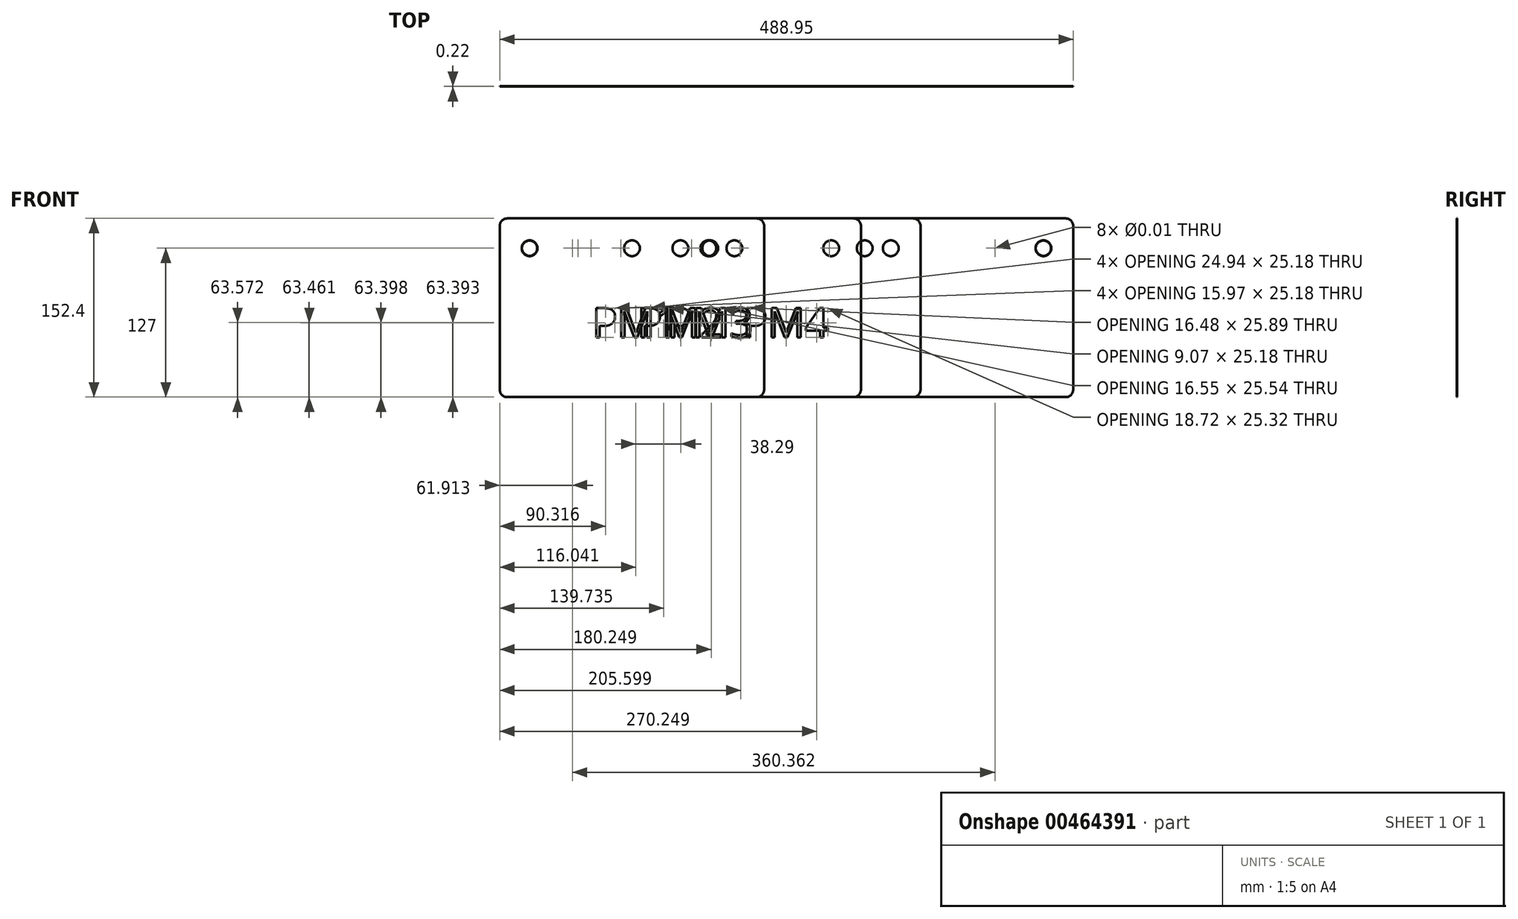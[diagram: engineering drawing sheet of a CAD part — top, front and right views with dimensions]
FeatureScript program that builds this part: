
annotation { "Feature Type Name" : "Feature", "Feature Type Description" : "" }
export const myFeature = defineFeature(function(context is Context, id is Id, definition is map)
    precondition{}
    {
        {
            assignVariable(context, id + "F0", {"name" : "Thickness", "anyValue" : .22});
        }
        {
            var Q0;
            Q0=qCreatedBy(makeId("Front.planeOp"),FACE);
            var sketch = newSketch(context, id + "F1", { "sketchPlane" : qUnion([Q0])});
            skLineSegment(sketch, "E0.bottom", {"start": v(0, -152.4) * mm, "end": v(488.95, -152.4) * mm});
            skLineSegment(sketch, "E0.top", {"start": v(0, 0) * mm, "end": v(488.95, 0) * mm});
            skLineSegment(sketch, "E0.left", {"start": v(0, -152.4) * mm, "end": v(0, 0) * mm});
            skLineSegment(sketch, "E0.right", {"start": v(488.95, -152.4) * mm, "end": v(488.95, 0) * mm});
            skPoint(sketch, "E1", {"position": v(25.4, -25.4) * mm});
            skPoint(sketch, "E2", {"position": v(66.68, -25.4) * mm});
            skPoint(sketch, "E3", {"position": v(244.48, -25.4) * mm});
            skPoint(sketch, "E4", {"position": v(422.28, -25.4) * mm});
            skPoint(sketch, "E5", {"position": v(463.55, -25.4) * mm});
            skLineSegment(sketch, "E6", {"start": v(244.48, 0) * mm, "end": v(244.48, -152.4) * mm, "construction": true});
            skText(sketch, "E7", { "text": "PM4", "fontName": "OpenSans-Regular.ttf"});
            skPoint(sketch, "E8", {"position": v(177.8, -25.4) * mm});
            skPoint(sketch, "E9", {"position": v(311.15, -25.4) * mm});
            const initialGuessF1  = {"E7": [0.20706, -0.1016, 1, 0, 0.0254]};
            skSetInitialGuess(sketch, initialGuessF1);
            skSolve(sketch);
        }
        {
            var Q0;
            Q0=makeQuery(id+"F1.imprint","IMPRINT",FACE,{"disambiguationData":[TD([[makeQuery(id+"F1.imprint","IMPRINT",EDGE,{"derivedFrom":sQuery(id+"F1.wireOp",EDGE,"E0.bottom")}),1.0]])]});
            extrude(context, id + "F2", {"entities" : qUnion([Q0]), "oppositeDirection" : true, "depth" : (getVariable(context, 'Thickness')) * mm});
        }
        {
            var Q0;
            Q0=sQuery(id+"F1.wireOp",VERTEX,"E2");
            var Q1;
            Q1=sQuery(id+"F1.wireOp",VERTEX,"E4");
            var Q2;
            Q2=makeQuery(id+"F2.opExtrude","SWEPT_BODY",BODY,{"disambiguationData":[OSD([sQuery(id+"F1.wireOp",EDGE,"E0.bottom"),sQuery(id+"F1.wireOp",EDGE,"E0.top"),sQuery(id+"F1.wireOp",EDGE,"E0.left"),sQuery(id+"F1.wireOp",EDGE,"E0.right")])]});
            hole(context, id + "F3", {"style" : HoleStyle.SIMPLE, "endStyle" : HoleEndStyle.THROUGH, "standardTappedOrClearance" : lookupTablePath({ "standard" : "ANSI", "size" : "3/8 (0.38)", "type" : "Drilled" }), "standardBlindInLast" : lookupTablePath({ "standard" : "ANSI", "size" : "3/8", "type" : "Drilled" }), "holeDiameter" : 3 / 203.2 * mm, "isTappedThrough" : true, "tappedDepth" : 12.7 * mm, "tapClearance" : 3, "locations" : qUnion([Q0, Q1]), "scope" : qUnion([Q2])});
        }
        {
            var Q0;
            Q0=sQuery(id+"F1.wireOp",VERTEX,"E1");
            var Q1;
            Q1=sQuery(id+"F1.wireOp",VERTEX,"E5");
            var Q2;
            Q2=sQuery(id+"F1.wireOp",VERTEX,"E9");
            var Q3;
            Q3=sQuery(id+"F1.wireOp",VERTEX,"E8");
            var Q4;
            Q4=makeQuery(id+"F2.opExtrude","SWEPT_BODY",BODY,{"disambiguationData":[OSD([sQuery(id+"F1.wireOp",EDGE,"E0.bottom"),sQuery(id+"F1.wireOp",EDGE,"E0.top"),sQuery(id+"F1.wireOp",EDGE,"E0.left"),sQuery(id+"F1.wireOp",EDGE,"E0.right")])]});
            hole(context, id + "F4", {"style" : HoleStyle.C_SINK, "endStyle" : HoleEndStyle.THROUGH, "standardTappedOrClearance" : lookupTablePath({ "standard" : "ISO", "fit" : "Normal", "size" : "M6", "type" : "Clearance" }), "standardBlindInLast" : lookupTablePath({ "fit" : "Standard", "standard" : "ISO", "size" : "M6", "type" : "Clearance" }), "holeDiameter" : 6.6 * mm, "cSinkDiameter" : 13.44 * mm, "cSinkAngle" : 90 * degree, "isTappedThrough" : true, "tappedDepth" : 12.7 * mm, "tapClearance" : 3, "locations" : qUnion([Q0, Q1, Q2, Q3]), "scope" : qUnion([Q4])});
        }
        {
            var Q0;
            Q0=makeQuery(id+"F2.opExtrude","SWEPT_EDGE",EDGE,{"disambiguationData":[OSD([sQuery(id+"F1.wireOp",EDGE,"E0.top"),sQuery(id+"F1.wireOp",EDGE,"E0.left")])]});
            var Q1;
            Q1=makeQuery(id+"F2.opExtrude","SWEPT_EDGE",EDGE,{"disambiguationData":[OSD([sQuery(id+"F1.wireOp",EDGE,"E0.top"),sQuery(id+"F1.wireOp",EDGE,"E0.right")])]});
            var Q2;
            Q2=makeQuery(id+"F2.opExtrude","SWEPT_EDGE",EDGE,{"disambiguationData":[OSD([sQuery(id+"F1.wireOp",EDGE,"E0.bottom"),sQuery(id+"F1.wireOp",EDGE,"E0.right")])]});
            var Q3;
            Q3=makeQuery(id+"F2.opExtrude","SWEPT_EDGE",EDGE,{"disambiguationData":[OSD([sQuery(id+"F1.wireOp",EDGE,"E0.bottom"),sQuery(id+"F1.wireOp",EDGE,"E0.left")])]});
            fillet(context, id + "F5", {"entities" : qUnion([Q0, Q1, Q2, Q3]), "radius" : 6.35 * mm, "tangentPropagation" : true, "allowEdgeOverflow" : false});
        }
        {
            var Q0;
            Q0=qCreatedBy(makeId("Front.planeOp"),FACE);
            var sketch = newSketch(context, id + "F6", { "sketchPlane" : qUnion([Q0])});
            skLineSegment(sketch, "E10.bottom", {"start": v(0, -152.4) * mm, "end": v(358.77, -152.4) * mm});
            skLineSegment(sketch, "E10.top", {"start": v(0, 0) * mm, "end": v(358.78, 0) * mm});
            skLineSegment(sketch, "E10.left", {"start": v(0, -152.4) * mm, "end": v(0, 0) * mm});
            skLineSegment(sketch, "E10.right", {"start": v(358.78, -152.4) * mm, "end": v(358.78, 0) * mm});
            skLineSegment(sketch, "E11", {"start": v(179.39, 0) * mm, "end": v(179.39, -152.4) * mm, "construction": true});
            skPoint(sketch, "E12", {"position": v(25.4, -25.4) * mm});
            skPoint(sketch, "E13", {"position": v(77.79, -25.4) * mm});
            skPoint(sketch, "E14", {"position": v(179.39, -25.4) * mm});
            skPoint(sketch, "E15", {"position": v(280.99, -25.4) * mm});
            skPoint(sketch, "E16", {"position": v(333.38, -25.4) * mm});
            skText(sketch, "E17", { "text": "PM3", "fontName": "OpenSans-Regular.ttf"});
            const initialGuessF6  = {"E17": [0.14265, -0.1016, 1, 0, 0.0254]};
            skSetInitialGuess(sketch, initialGuessF6);
            skSolve(sketch);
        }
        {
            var Q0;
            Q0 = qSketchRegion(id + "F6", true);
            extrude(context, id + "F7", {"entities" : qUnion([Q0]), "oppositeDirection" : true, "depth" : (getVariable(context, 'Thickness')) * mm});
        }
        {
            var Q0;
            Q0=makeQuery(id+"F7.opExtrude","SWEPT_EDGE",EDGE,{"disambiguationData":[OSD([sQuery(id+"F6.wireOp",EDGE,"E10.top"),sQuery(id+"F6.wireOp",EDGE,"E10.left")])]});
            var Q1;
            Q1=makeQuery(id+"F7.opExtrude","SWEPT_EDGE",EDGE,{"disambiguationData":[OSD([sQuery(id+"F6.wireOp",EDGE,"E10.top"),sQuery(id+"F6.wireOp",EDGE,"E10.right")])]});
            var Q2;
            Q2=makeQuery(id+"F7.opExtrude","SWEPT_EDGE",EDGE,{"disambiguationData":[OSD([sQuery(id+"F6.wireOp",EDGE,"E10.bottom"),sQuery(id+"F6.wireOp",EDGE,"E10.right")])]});
            var Q3;
            Q3=makeQuery(id+"F7.opExtrude","SWEPT_EDGE",EDGE,{"disambiguationData":[OSD([sQuery(id+"F6.wireOp",EDGE,"E10.bottom"),sQuery(id+"F6.wireOp",EDGE,"E10.left")])]});
            fillet(context, id + "F8", {"entities" : qUnion([Q0, Q1, Q2, Q3]), "radius" : 6.35 * mm, "tangentPropagation" : true, "allowEdgeOverflow" : false});
        }
        {
            var Q0;
            Q0=sQuery(id+"F6.wireOp",VERTEX,"E15");
            var Q1;
            Q1=sQuery(id+"F6.wireOp",VERTEX,"E13");
            var Q2;
            Q2=makeQuery(id+"F7.opExtrude","SWEPT_BODY",BODY,{"disambiguationData":[OSD([sQuery(id+"F6.wireOp",EDGE,"E10.bottom"),sQuery(id+"F6.wireOp",EDGE,"E10.top"),sQuery(id+"F6.wireOp",EDGE,"E10.left"),sQuery(id+"F6.wireOp",EDGE,"E10.right")])]});
            hole(context, id + "F9", {"style" : HoleStyle.SIMPLE, "endStyle" : HoleEndStyle.THROUGH, "standardTappedOrClearance" : lookupTablePath({ "standard" : "ANSI", "size" : "3/8 (0.38)", "type" : "Drilled" }), "standardBlindInLast" : lookupTablePath({ "standard" : "ANSI", "size" : "3/8", "type" : "Drilled" }), "holeDiameter" : 3 / 203.2 * mm, "isTappedThrough" : true, "tappedDepth" : 12.7 * mm, "tapClearance" : 3, "locations" : qUnion([Q0, Q1]), "scope" : qUnion([Q2])});
        }
        {
            var Q0;
            Q0=sQuery(id+"F6.wireOp",VERTEX,"E12");
            var Q1;
            Q1=sQuery(id+"F6.wireOp",VERTEX,"E14");
            var Q2;
            Q2=sQuery(id+"F6.wireOp",VERTEX,"E16");
            var Q3;
            Q3=makeQuery(id+"F7.opExtrude","SWEPT_BODY",BODY,{"disambiguationData":[OSD([sQuery(id+"F6.wireOp",EDGE,"E10.bottom"),sQuery(id+"F6.wireOp",EDGE,"E10.top"),sQuery(id+"F6.wireOp",EDGE,"E10.left"),sQuery(id+"F6.wireOp",EDGE,"E10.right")])]});
            hole(context, id + "F10", {"style" : HoleStyle.C_SINK, "endStyle" : HoleEndStyle.THROUGH, "standardTappedOrClearance" : lookupTablePath({ "standard" : "ISO", "fit" : "Normal", "size" : "M6", "type" : "Clearance" }), "standardBlindInLast" : lookupTablePath({ "fit" : "Standard", "standard" : "ISO", "size" : "M6", "type" : "Clearance" }), "holeDiameter" : 6.6 * mm, "cSinkDiameter" : 13.44 * mm, "cSinkAngle" : 90 * degree, "isTappedThrough" : true, "tappedDepth" : 12.7 * mm, "tapClearance" : 3, "locations" : qUnion([Q0, Q1, Q2]), "scope" : qUnion([Q3])});
        }
        {
            var Q0;
            Q0=qCreatedBy(makeId("Front.planeOp"),FACE);
            var sketch = newSketch(context, id + "F11", { "sketchPlane" : qUnion([Q0])});
            skLineSegment(sketch, "E18.bottom", {"start": v(0, -152.4) * mm, "end": v(307.97, -152.4) * mm});
            skLineSegment(sketch, "E18.top", {"start": v(0, 0) * mm, "end": v(307.97, 0) * mm});
            skLineSegment(sketch, "E18.left", {"start": v(0, -152.4) * mm, "end": v(0, 0) * mm});
            skLineSegment(sketch, "E18.right", {"start": v(307.98, -152.4) * mm, "end": v(307.98, 0) * mm});
            skLineSegment(sketch, "E19", {"start": v(153.99, 0) * mm, "end": v(153.99, -152.4) * mm, "construction": true});
            skPoint(sketch, "E20", {"position": v(103.19, -25.4) * mm});
            skPoint(sketch, "E21", {"position": v(204.79, -25.4) * mm});
            skPoint(sketch, "E22", {"position": v(25.4, -25.4) * mm});
            skPoint(sketch, "E23", {"position": v(153.99, -25.4) * mm});
            skPoint(sketch, "E24", {"position": v(282.57, -25.4) * mm});
            skText(sketch, "E25", { "text": "PM2", "fontName": "OpenSans-Regular.ttf"});
            const initialGuessF11  = {"E25": [0.11716, -0.1016, 1, 0, 0.0254]};
            skSetInitialGuess(sketch, initialGuessF11);
            skSolve(sketch);
        }
        {
            var Q0;
            Q0=makeQuery(id+"F11.imprint","IMPRINT",FACE,{"disambiguationData":[TD([[makeQuery(id+"F11.imprint","IMPRINT",EDGE,{"derivedFrom":sQuery(id+"F11.wireOp",EDGE,"E18.bottom")}),1.0]])]});
            extrude(context, id + "F12", {"entities" : qUnion([Q0]), "oppositeDirection" : true, "depth" : (getVariable(context, 'Thickness')) * mm});
        }
        {
            var Q0;
            Q0=makeQuery(id+"F12.opExtrude","SWEPT_EDGE",EDGE,{"disambiguationData":[OSD([sQuery(id+"F11.wireOp",EDGE,"E18.top"),sQuery(id+"F11.wireOp",EDGE,"E18.left")])]});
            var Q1;
            Q1=makeQuery(id+"F12.opExtrude","SWEPT_EDGE",EDGE,{"disambiguationData":[OSD([sQuery(id+"F11.wireOp",EDGE,"E18.top"),sQuery(id+"F11.wireOp",EDGE,"E18.right")])]});
            var Q2;
            Q2=makeQuery(id+"F12.opExtrude","SWEPT_EDGE",EDGE,{"disambiguationData":[OSD([sQuery(id+"F11.wireOp",EDGE,"E18.bottom"),sQuery(id+"F11.wireOp",EDGE,"E18.right")])]});
            var Q3;
            Q3=makeQuery(id+"F12.opExtrude","SWEPT_EDGE",EDGE,{"disambiguationData":[OSD([sQuery(id+"F11.wireOp",EDGE,"E18.bottom"),sQuery(id+"F11.wireOp",EDGE,"E18.left")])]});
            fillet(context, id + "F13", {"entities" : qUnion([Q0, Q1, Q2, Q3]), "radius" : 6.35 * mm, "tangentPropagation" : true, "allowEdgeOverflow" : false});
        }
        {
            var Q0;
            Q0=sQuery(id+"F11.wireOp",VERTEX,"E21");
            var Q1;
            Q1=sQuery(id+"F11.wireOp",VERTEX,"E20");
            var Q2;
            Q2=makeQuery(id+"F12.opExtrude","SWEPT_BODY",BODY,{"disambiguationData":[OSD([sQuery(id+"F11.wireOp",EDGE,"E18.bottom"),sQuery(id+"F11.wireOp",EDGE,"E18.top"),sQuery(id+"F11.wireOp",EDGE,"E18.left"),sQuery(id+"F11.wireOp",EDGE,"E18.right")])]});
            hole(context, id + "F14", {"style" : HoleStyle.SIMPLE, "endStyle" : HoleEndStyle.THROUGH, "standardTappedOrClearance" : lookupTablePath({ "standard" : "ANSI", "size" : "3/8 (0.38)", "type" : "Drilled" }), "standardBlindInLast" : lookupTablePath({ "standard" : "ANSI", "size" : "3/8", "type" : "Drilled" }), "holeDiameter" : 3 / 203.2 * mm, "isTappedThrough" : true, "tappedDepth" : 12.7 * mm, "tapClearance" : 3, "locations" : qUnion([Q0, Q1]), "scope" : qUnion([Q2])});
        }
        {
            var Q0;
            Q0=sQuery(id+"F11.wireOp",VERTEX,"E22");
            var Q1;
            Q1=sQuery(id+"F11.wireOp",VERTEX,"E23");
            var Q2;
            Q2=sQuery(id+"F11.wireOp",VERTEX,"E24");
            var Q3;
            Q3=makeQuery(id+"F12.opExtrude","SWEPT_BODY",BODY,{"disambiguationData":[OSD([sQuery(id+"F11.wireOp",EDGE,"E18.bottom"),sQuery(id+"F11.wireOp",EDGE,"E18.top"),sQuery(id+"F11.wireOp",EDGE,"E18.left"),sQuery(id+"F11.wireOp",EDGE,"E18.right"),sQuery(id+"F11.wireOp",EDGE,"E25.sketch_text.stroke-0"),sQuery(id+"F11.wireOp",EDGE,"E25.sketch_text.stroke-1"),sQuery(id+"F11.wireOp",EDGE,"E25.sketch_text.stroke-2"),sQuery(id+"F11.wireOp",EDGE,"E25.sketch_text.stroke-3"),sQuery(id+"F11.wireOp",EDGE,"E25.sketch_text.stroke-4"),sQuery(id+"F11.wireOp",EDGE,"E25.sketch_text.stroke-5"),sQuery(id+"F11.wireOp",EDGE,"E25.sketch_text.stroke-6"),sQuery(id+"F11.wireOp",EDGE,"E25.sketch_text.stroke-7"),sQuery(id+"F11.wireOp",EDGE,"E25.sketch_text.stroke-15"),sQuery(id+"F11.wireOp",EDGE,"E25.sketch_text.stroke-16"),sQuery(id+"F11.wireOp",EDGE,"E25.sketch_text.stroke-17"),sQuery(id+"F11.wireOp",EDGE,"E25.sketch_text.stroke-18"),sQuery(id+"F11.wireOp",EDGE,"E25.sketch_text.stroke-19"),sQuery(id+"F11.wireOp",EDGE,"E25.sketch_text.stroke-20"),sQuery(id+"F11.wireOp",EDGE,"E25.sketch_text.stroke-21"),sQuery(id+"F11.wireOp",EDGE,"E25.sketch_text.stroke-22"),sQuery(id+"F11.wireOp",EDGE,"E25.sketch_text.stroke-23"),sQuery(id+"F11.wireOp",EDGE,"E25.sketch_text.stroke-24"),sQuery(id+"F11.wireOp",EDGE,"E25.sketch_text.stroke-25"),sQuery(id+"F11.wireOp",EDGE,"E25.sketch_text.stroke-26"),sQuery(id+"F11.wireOp",EDGE,"E25.sketch_text.stroke-27"),sQuery(id+"F11.wireOp",EDGE,"E25.sketch_text.stroke-28"),sQuery(id+"F11.wireOp",EDGE,"E25.sketch_text.stroke-29"),sQuery(id+"F11.wireOp",EDGE,"E25.sketch_text.stroke-30"),sQuery(id+"F11.wireOp",EDGE,"E25.sketch_text.stroke-31"),sQuery(id+"F11.wireOp",EDGE,"E25.sketch_text.stroke-32"),sQuery(id+"F11.wireOp",EDGE,"E25.sketch_text.stroke-33"),sQuery(id+"F11.wireOp",EDGE,"E25.sketch_text.stroke-34"),sQuery(id+"F11.wireOp",EDGE,"E25.sketch_text.stroke-35"),sQuery(id+"F11.wireOp",EDGE,"E25.sketch_text.stroke-36"),sQuery(id+"F11.wireOp",EDGE,"E25.sketch_text.stroke-37"),sQuery(id+"F11.wireOp",EDGE,"E25.sketch_text.stroke-38"),sQuery(id+"F11.wireOp",EDGE,"E25.sketch_text.stroke-39"),sQuery(id+"F11.wireOp",EDGE,"E25.sketch_text.stroke-40"),sQuery(id+"F11.wireOp",EDGE,"E25.sketch_text.stroke-41"),sQuery(id+"F11.wireOp",EDGE,"E25.sketch_text.stroke-42"),sQuery(id+"F11.wireOp",EDGE,"E25.sketch_text.stroke-43"),sQuery(id+"F11.wireOp",EDGE,"E25.sketch_text.stroke-44"),sQuery(id+"F11.wireOp",EDGE,"E25.sketch_text.stroke-45"),sQuery(id+"F11.wireOp",EDGE,"E25.sketch_text.stroke-46"),sQuery(id+"F11.wireOp",EDGE,"E25.sketch_text.stroke-47"),sQuery(id+"F11.wireOp",EDGE,"E25.sketch_text.stroke-48"),sQuery(id+"F11.wireOp",EDGE,"E25.sketch_text.stroke-49"),sQuery(id+"F11.wireOp",EDGE,"E25.sketch_text.stroke-50"),sQuery(id+"F11.wireOp",EDGE,"E25.sketch_text.stroke-51"),sQuery(id+"F11.wireOp",EDGE,"E25.sketch_text.stroke-52")])]});
            hole(context, id + "F15", {"style" : HoleStyle.C_SINK, "endStyle" : HoleEndStyle.THROUGH, "standardTappedOrClearance" : lookupTablePath({ "standard" : "ISO", "fit" : "Normal", "size" : "M6", "type" : "Clearance" }), "standardBlindInLast" : lookupTablePath({ "fit" : "Standard", "standard" : "ISO", "size" : "M6", "type" : "Clearance" }), "holeDiameter" : 6.6 * mm, "cSinkDiameter" : 13.44 * mm, "cSinkAngle" : 90 * degree, "isTappedThrough" : true, "tappedDepth" : 12.7 * mm, "tapClearance" : 3, "locations" : qUnion([Q0, Q1, Q2]), "scope" : qUnion([Q3])});
        }
        {
            var Q0;
            Q0=qCreatedBy(makeId("Front.planeOp"),FACE);
            var sketch = newSketch(context, id + "F16", { "sketchPlane" : qUnion([Q0])});
            skLineSegment(sketch, "E26.bottom", {"start": v(0, -152.4) * mm, "end": v(225.42, -152.4) * mm});
            skLineSegment(sketch, "E26.top", {"start": v(0, 0) * mm, "end": v(225.42, 0) * mm});
            skLineSegment(sketch, "E26.left", {"start": v(0, -152.4) * mm, "end": v(0, 0) * mm});
            skLineSegment(sketch, "E26.right", {"start": v(225.42, -152.4) * mm, "end": v(225.43, 0) * mm});
            skLineSegment(sketch, "E27", {"start": v(112.71, 0) * mm, "end": v(112.71, -152.4) * mm, "construction": true});
            skPoint(sketch, "E28", {"position": v(61.91, -25.4) * mm});
            skPoint(sketch, "E29", {"position": v(163.51, -25.4) * mm});
            skPoint(sketch, "E30", {"position": v(25.4, -25.4) * mm});
            skPoint(sketch, "E31", {"position": v(112.71, -25.4) * mm});
            skPoint(sketch, "E32", {"position": v(200.02, -25.4) * mm});
            skText(sketch, "E33", { "text": "PM1", "fontName": "OpenSans-Regular.ttf"});
            const initialGuessF16  = {"E33": [0.07887, -0.1016, 1, 0, 0.0254]};
            skSetInitialGuess(sketch, initialGuessF16);
            skSolve(sketch);
        }
        {
            var Q0;
            Q0 = qSketchRegion(id + "F16", true);
            extrude(context, id + "F17", {"entities" : qUnion([Q0]), "oppositeDirection" : true, "depth" : (getVariable(context, 'Thickness')) * mm});
        }
        {
            var Q0;
            Q0=makeQuery(id+"F17.opExtrude","SWEPT_EDGE",EDGE,{"disambiguationData":[OSD([sQuery(id+"F16.wireOp",EDGE,"E26.top"),sQuery(id+"F16.wireOp",EDGE,"E26.left")])]});
            var Q1;
            Q1=makeQuery(id+"F17.opExtrude","SWEPT_EDGE",EDGE,{"disambiguationData":[OSD([sQuery(id+"F16.wireOp",EDGE,"E26.top"),sQuery(id+"F16.wireOp",EDGE,"E26.right")])]});
            var Q2;
            Q2=makeQuery(id+"F17.opExtrude","SWEPT_EDGE",EDGE,{"disambiguationData":[OSD([sQuery(id+"F16.wireOp",EDGE,"E26.bottom"),sQuery(id+"F16.wireOp",EDGE,"E26.right")])]});
            var Q3;
            Q3=makeQuery(id+"F17.opExtrude","SWEPT_EDGE",EDGE,{"disambiguationData":[OSD([sQuery(id+"F16.wireOp",EDGE,"E26.bottom"),sQuery(id+"F16.wireOp",EDGE,"E26.left")])]});
            fillet(context, id + "F18", {"entities" : qUnion([Q0, Q1, Q2, Q3]), "radius" : 6.35 * mm, "tangentPropagation" : true, "allowEdgeOverflow" : false});
        }
        {
            var Q0;
            Q0=sQuery(id+"F16.wireOp",VERTEX,"E30");
            var Q1;
            Q1=sQuery(id+"F16.wireOp",VERTEX,"E31");
            var Q2;
            Q2=sQuery(id+"F16.wireOp",VERTEX,"E32");
            var Q3;
            Q3=makeQuery(id+"F17.opExtrude","SWEPT_BODY",BODY,{"disambiguationData":[OSD([sQuery(id+"F16.wireOp",EDGE,"E26.bottom"),sQuery(id+"F16.wireOp",EDGE,"E26.top"),sQuery(id+"F16.wireOp",EDGE,"E26.left"),sQuery(id+"F16.wireOp",EDGE,"E26.right"),sQuery(id+"F16.wireOp",EDGE,"E33.sketch_text.stroke-0"),sQuery(id+"F16.wireOp",EDGE,"E33.sketch_text.stroke-1"),sQuery(id+"F16.wireOp",EDGE,"E33.sketch_text.stroke-2"),sQuery(id+"F16.wireOp",EDGE,"E33.sketch_text.stroke-3"),sQuery(id+"F16.wireOp",EDGE,"E33.sketch_text.stroke-4"),sQuery(id+"F16.wireOp",EDGE,"E33.sketch_text.stroke-5"),sQuery(id+"F16.wireOp",EDGE,"E33.sketch_text.stroke-6"),sQuery(id+"F16.wireOp",EDGE,"E33.sketch_text.stroke-7"),sQuery(id+"F16.wireOp",EDGE,"E33.sketch_text.stroke-15"),sQuery(id+"F16.wireOp",EDGE,"E33.sketch_text.stroke-16"),sQuery(id+"F16.wireOp",EDGE,"E33.sketch_text.stroke-17"),sQuery(id+"F16.wireOp",EDGE,"E33.sketch_text.stroke-18"),sQuery(id+"F16.wireOp",EDGE,"E33.sketch_text.stroke-19"),sQuery(id+"F16.wireOp",EDGE,"E33.sketch_text.stroke-20"),sQuery(id+"F16.wireOp",EDGE,"E33.sketch_text.stroke-21"),sQuery(id+"F16.wireOp",EDGE,"E33.sketch_text.stroke-22"),sQuery(id+"F16.wireOp",EDGE,"E33.sketch_text.stroke-23"),sQuery(id+"F16.wireOp",EDGE,"E33.sketch_text.stroke-24"),sQuery(id+"F16.wireOp",EDGE,"E33.sketch_text.stroke-25"),sQuery(id+"F16.wireOp",EDGE,"E33.sketch_text.stroke-26"),sQuery(id+"F16.wireOp",EDGE,"E33.sketch_text.stroke-27"),sQuery(id+"F16.wireOp",EDGE,"E33.sketch_text.stroke-28"),sQuery(id+"F16.wireOp",EDGE,"E33.sketch_text.stroke-29"),sQuery(id+"F16.wireOp",EDGE,"E33.sketch_text.stroke-30"),sQuery(id+"F16.wireOp",EDGE,"E33.sketch_text.stroke-31"),sQuery(id+"F16.wireOp",EDGE,"E33.sketch_text.stroke-32"),sQuery(id+"F16.wireOp",EDGE,"E33.sketch_text.stroke-33"),sQuery(id+"F16.wireOp",EDGE,"E33.sketch_text.stroke-34"),sQuery(id+"F16.wireOp",EDGE,"E33.sketch_text.stroke-35"),sQuery(id+"F16.wireOp",EDGE,"E33.sketch_text.stroke-36"),sQuery(id+"F16.wireOp",EDGE,"E33.sketch_text.stroke-37"),sQuery(id+"F16.wireOp",EDGE,"E33.sketch_text.stroke-38"),sQuery(id+"F16.wireOp",EDGE,"E33.sketch_text.stroke-39"),sQuery(id+"F16.wireOp",EDGE,"E33.sketch_text.stroke-40"),sQuery(id+"F16.wireOp",EDGE,"E33.sketch_text.stroke-41")])]});
            hole(context, id + "F19", {"style" : HoleStyle.C_SINK, "endStyle" : HoleEndStyle.THROUGH, "standardTappedOrClearance" : lookupTablePath({ "standard" : "ISO", "fit" : "Normal", "size" : "M6", "type" : "Clearance" }), "standardBlindInLast" : lookupTablePath({ "fit" : "Standard", "standard" : "ISO", "size" : "M6", "type" : "Clearance" }), "holeDiameter" : 6.6 * mm, "cSinkDiameter" : 13.44 * mm, "cSinkAngle" : 90 * degree, "isTappedThrough" : true, "tappedDepth" : 12.7 * mm, "tapClearance" : 3, "locations" : qUnion([Q0, Q1, Q2]), "scope" : qUnion([Q3])});
        }
        {
            var Q0;
            Q0=sQuery(id+"F16.wireOp",VERTEX,"E29");
            var Q1;
            Q1=sQuery(id+"F16.wireOp",VERTEX,"E28");
            var Q2;
            Q2=makeQuery(id+"F17.opExtrude","SWEPT_BODY",BODY,{"disambiguationData":[OSD([sQuery(id+"F16.wireOp",EDGE,"E26.bottom"),sQuery(id+"F16.wireOp",EDGE,"E26.top"),sQuery(id+"F16.wireOp",EDGE,"E26.left"),sQuery(id+"F16.wireOp",EDGE,"E26.right"),sQuery(id+"F16.wireOp",EDGE,"E33.sketch_text.stroke-0"),sQuery(id+"F16.wireOp",EDGE,"E33.sketch_text.stroke-1"),sQuery(id+"F16.wireOp",EDGE,"E33.sketch_text.stroke-2"),sQuery(id+"F16.wireOp",EDGE,"E33.sketch_text.stroke-3"),sQuery(id+"F16.wireOp",EDGE,"E33.sketch_text.stroke-4"),sQuery(id+"F16.wireOp",EDGE,"E33.sketch_text.stroke-5"),sQuery(id+"F16.wireOp",EDGE,"E33.sketch_text.stroke-6"),sQuery(id+"F16.wireOp",EDGE,"E33.sketch_text.stroke-7"),sQuery(id+"F16.wireOp",EDGE,"E33.sketch_text.stroke-15"),sQuery(id+"F16.wireOp",EDGE,"E33.sketch_text.stroke-16"),sQuery(id+"F16.wireOp",EDGE,"E33.sketch_text.stroke-17"),sQuery(id+"F16.wireOp",EDGE,"E33.sketch_text.stroke-18"),sQuery(id+"F16.wireOp",EDGE,"E33.sketch_text.stroke-19"),sQuery(id+"F16.wireOp",EDGE,"E33.sketch_text.stroke-20"),sQuery(id+"F16.wireOp",EDGE,"E33.sketch_text.stroke-21"),sQuery(id+"F16.wireOp",EDGE,"E33.sketch_text.stroke-22"),sQuery(id+"F16.wireOp",EDGE,"E33.sketch_text.stroke-23"),sQuery(id+"F16.wireOp",EDGE,"E33.sketch_text.stroke-24"),sQuery(id+"F16.wireOp",EDGE,"E33.sketch_text.stroke-25"),sQuery(id+"F16.wireOp",EDGE,"E33.sketch_text.stroke-26"),sQuery(id+"F16.wireOp",EDGE,"E33.sketch_text.stroke-27"),sQuery(id+"F16.wireOp",EDGE,"E33.sketch_text.stroke-28"),sQuery(id+"F16.wireOp",EDGE,"E33.sketch_text.stroke-29"),sQuery(id+"F16.wireOp",EDGE,"E33.sketch_text.stroke-30"),sQuery(id+"F16.wireOp",EDGE,"E33.sketch_text.stroke-31"),sQuery(id+"F16.wireOp",EDGE,"E33.sketch_text.stroke-32"),sQuery(id+"F16.wireOp",EDGE,"E33.sketch_text.stroke-33"),sQuery(id+"F16.wireOp",EDGE,"E33.sketch_text.stroke-34"),sQuery(id+"F16.wireOp",EDGE,"E33.sketch_text.stroke-35"),sQuery(id+"F16.wireOp",EDGE,"E33.sketch_text.stroke-36"),sQuery(id+"F16.wireOp",EDGE,"E33.sketch_text.stroke-37"),sQuery(id+"F16.wireOp",EDGE,"E33.sketch_text.stroke-38"),sQuery(id+"F16.wireOp",EDGE,"E33.sketch_text.stroke-39"),sQuery(id+"F16.wireOp",EDGE,"E33.sketch_text.stroke-40"),sQuery(id+"F16.wireOp",EDGE,"E33.sketch_text.stroke-41")])]});
            hole(context, id + "F20", {"style" : HoleStyle.SIMPLE, "endStyle" : HoleEndStyle.THROUGH, "standardTappedOrClearance" : lookupTablePath({ "standard" : "ANSI", "size" : "3/8 (0.38)", "type" : "Drilled" }), "standardBlindInLast" : lookupTablePath({ "standard" : "ANSI", "size" : "3/8", "type" : "Drilled" }), "holeDiameter" : 3 / 203.2 * mm, "isTappedThrough" : true, "tappedDepth" : 12.7 * mm, "tapClearance" : 3, "locations" : qUnion([Q0, Q1]), "scope" : qUnion([Q2])});
        }
    });
